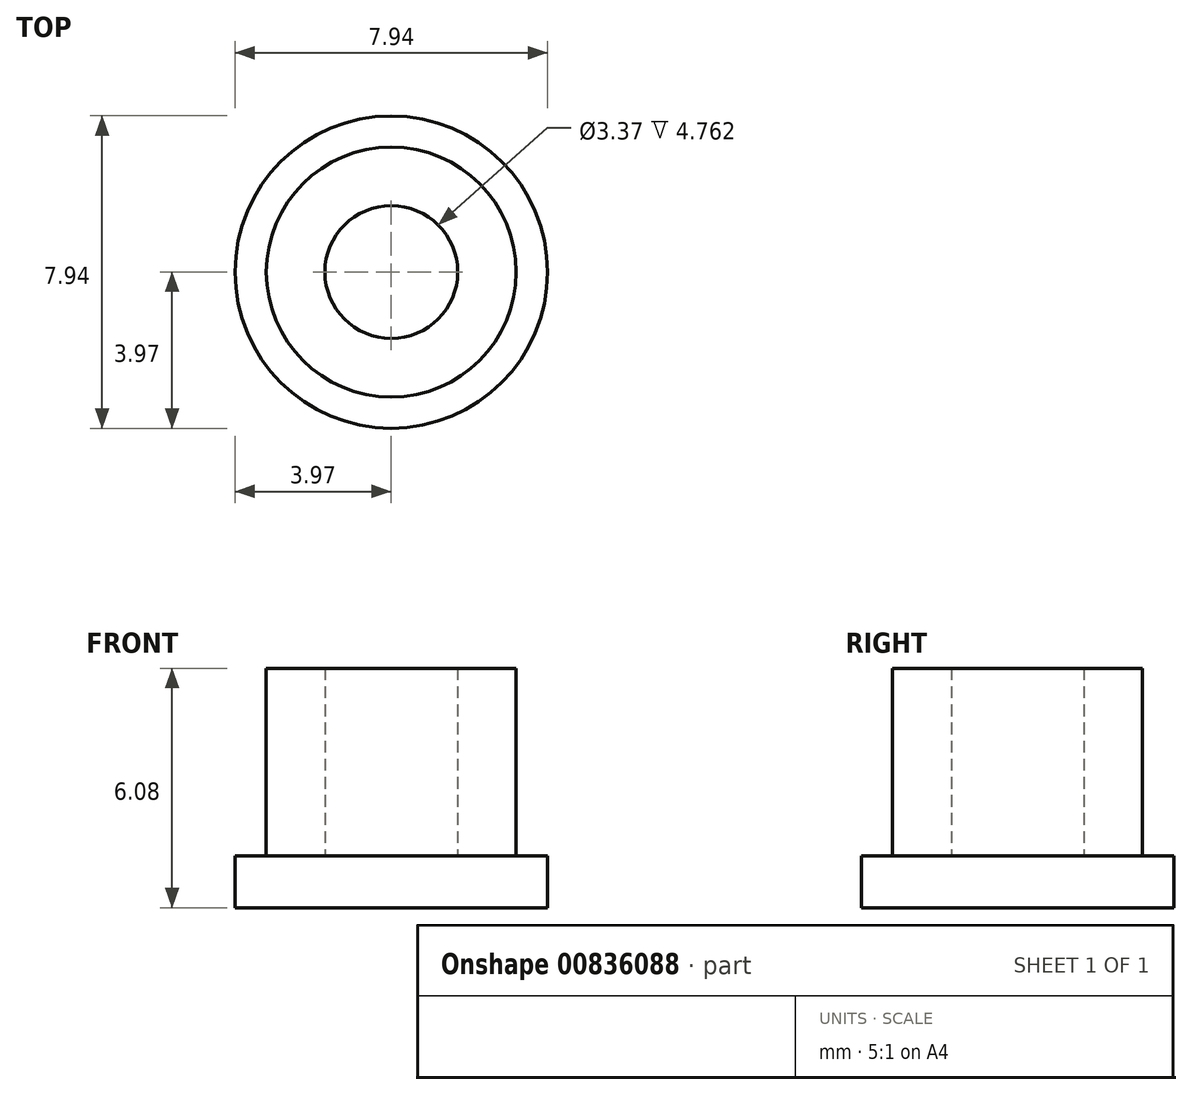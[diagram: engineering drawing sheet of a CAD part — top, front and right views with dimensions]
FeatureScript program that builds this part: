
annotation { "Feature Type Name" : "Feature", "Feature Type Description" : "" }
export const myFeature = defineFeature(function(context is Context, id is Id, definition is map)
    precondition{}
    {
        {
            var Q0;
            Q0=qCreatedBy(makeId("Top.planeOp"),FACE);
            var sketch = newSketch(context, id + "F0", { "sketchPlane" : qUnion([Q0])});
            skCircle(sketch, "E0", {"center": v(0, 0) * mm, "radius": 8.93 * mm});
            skCircle(sketch, "E1", {"center": v(0, 0) * mm, "radius": 3.97 * mm});
            skCircle(sketch, "E2", {"center": v(0, 0) * mm, "radius": 3.18 * mm});
            skCircle(sketch, "E3", {"center": v(0, 0) * mm, "radius": 1.69 * mm});
            skSolve(sketch);
        }
        {
            var Q0;
            Q0=makeQuery(id+"F0.imprint","IMPRINT",FACE,{"disambiguationData":[TD([[makeQuery(id+"F0.imprint","IMPRINT",EDGE,{"derivedFrom":sQuery(id+"F0.wireOp",EDGE,"E3")}),1.0]])]});
            var Q1;
            Q1=makeQuery(id+"F0.imprint","IMPRINT",FACE,{"disambiguationData":[TD([[makeQuery(id+"F0.imprint","IMPRINT",EDGE,{"derivedFrom":sQuery(id+"F0.wireOp",EDGE,"E2")}),1.0]])]});
            var Q2;
            Q2=makeQuery(id+"F0.imprint","IMPRINT",FACE,{"disambiguationData":[TD([[makeQuery(id+"F0.imprint","IMPRINT",EDGE,{"derivedFrom":sQuery(id+"F0.wireOp",EDGE,"E1")}),1.0]])]});
            var Q3;
            Q3=makeQuery(id+"F0.imprint","IMPRINT",FACE,{"disambiguationData":[TD([[makeQuery(id+"F0.imprint","IMPRINT",EDGE,{"derivedFrom":sQuery(id+"F0.wireOp",EDGE,"E0")}),1.0]])]});
            extrude(context, id + "F1", {"entities" : qUnion([Q0, Q1, Q2, Q3]), "oppositeDirection" : true, "depth" : 1 / 203.2 * mm, "offsetDistance" : 25.4 * mm});
        }
        {
            var Q0;
            Q0=makeQuery(id+"F0.imprint","IMPRINT",FACE,{"disambiguationData":[TD([[makeQuery(id+"F0.imprint","IMPRINT",EDGE,{"derivedFrom":sQuery(id+"F0.wireOp",EDGE,"E1")}),1.0]])]});
            var Q1;
            Q1=makeQuery(id+"F0.imprint","IMPRINT",FACE,{"disambiguationData":[TD([[makeQuery(id+"F0.imprint","IMPRINT",EDGE,{"derivedFrom":sQuery(id+"F0.wireOp",EDGE,"E2")}),1.0]])]});
            var Q2;
            Q2=makeQuery(id+"F0.imprint","IMPRINT",FACE,{"disambiguationData":[TD([[makeQuery(id+"F0.imprint","IMPRINT",EDGE,{"derivedFrom":sQuery(id+"F0.wireOp",EDGE,"E3")}),1.0]])]});
            extrude(context, id + "F2", {"entities" : qUnion([Q0, Q1, Q2]), "operationType" : NewBodyOperationType.ADD, "depth" : 1.32 * mm, "offsetDistance" : 25.4 * mm});
        }
        {
            var Q0;
            Q0=makeQuery(id+"F0.imprint","IMPRINT",FACE,{"disambiguationData":[TD([[makeQuery(id+"F0.imprint","IMPRINT",EDGE,{"derivedFrom":sQuery(id+"F0.wireOp",EDGE,"E2")}),1.0]])]});
            extrude(context, id + "F3", {"entities" : qUnion([Q0]), "operationType" : NewBodyOperationType.ADD, "depth" : 6.08 * mm, "offsetDistance" : 25.4 * mm});
        }
        {
            var Q1;
            Q1=makeQuery(id+"F1.opExtrude","CAP_FACE",FACE,{"disambiguationData":[OSD([sQuery(id+"F0.wireOp",EDGE,"E0")])],"isStart":false});
            var Q2;
            Q2=sQuery(id+"F0.wireOp",VERTEX,"E0.center");
            loft(context, id + "F4", {"operationType" : NewBodyOperationType.REMOVE, "sheetProfilesArray" : [{ "sheetProfileEntities" : qUnion([Q1]) }, { "sheetProfileEntities" : qUnion([Q2]) }]});
        }
    });
